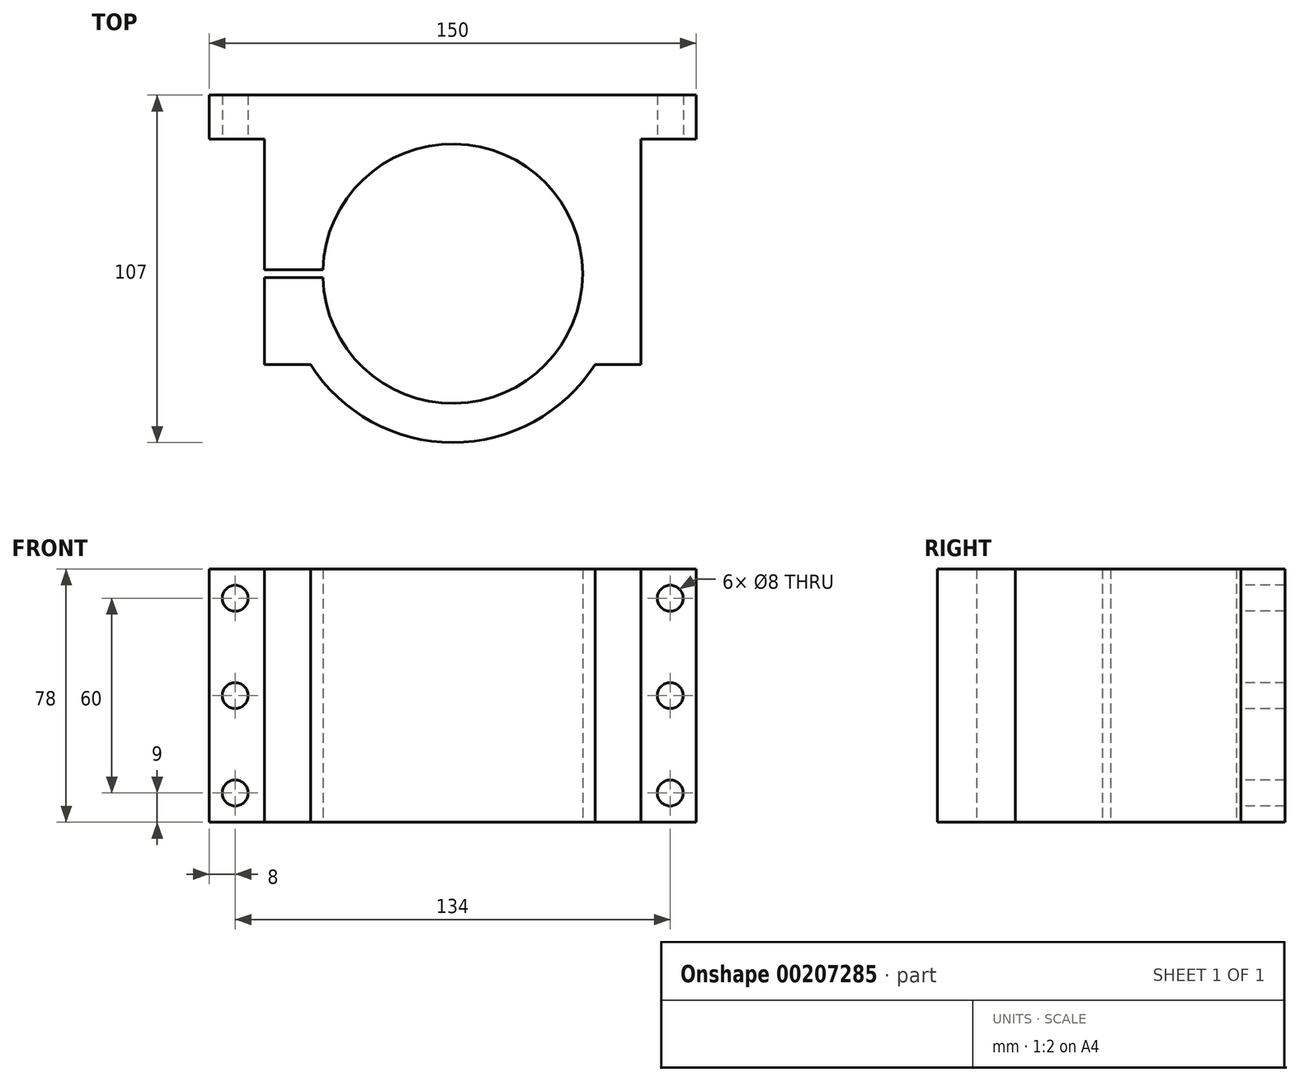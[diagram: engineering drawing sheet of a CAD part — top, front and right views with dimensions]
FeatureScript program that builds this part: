
annotation { "Feature Type Name" : "Feature", "Feature Type Description" : "" }
export const myFeature = defineFeature(function(context is Context, id is Id, definition is map)
    precondition{}
    {
        {
            var Q0;
            Q0=qCreatedBy(makeId("Top.planeOp"),FACE);
            var sketch = newSketch(context, id + "F0", { "sketchPlane" : qUnion([Q0])});
            skArc(sketch, "E0", {"start": v(-39.98, -1.25) * mm, "mid": v(40, 0) * mm, "end": v(-39.98, 1.25) * mm});
            skArc(sketch, "E1", {"start": v(-43.82, -28) * mm, "mid": v(0, -52) * mm, "end": v(43.82, -28) * mm});
            skLineSegment(sketch, "E2", {"start": v(-75, 55) * mm, "end": v(75, 55) * mm});
            skLineSegment(sketch, "E3", {"start": v(75, 55) * mm, "end": v(75, 41.5) * mm});
            skLineSegment(sketch, "E4", {"start": v(75, 41.5) * mm, "end": v(58, 41.5) * mm});
            skLineSegment(sketch, "E5", {"start": v(58, 41.5) * mm, "end": v(58, -28) * mm});
            skLineSegment(sketch, "E6", {"start": v(58, -28) * mm, "end": v(43.82, -28) * mm});
            skLineSegment(sketch, "E7", {"start": v(-58, -28) * mm, "end": v(-58, -1.25) * mm});
            skLineSegment(sketch, "E8", {"start": v(-58, 41.5) * mm, "end": v(-75, 41.5) * mm});
            skLineSegment(sketch, "E9", {"start": v(-75, 41.5) * mm, "end": v(-75, 55) * mm});
            skLineSegment(sketch, "E10", {"start": v(0, 0) * mm, "end": v(0, 55) * mm, "construction": true});
            skLineSegment(sketch, "E11.trimOffspring", {"start": v(-43.82, -28) * mm, "end": v(-58, -28) * mm});
            skLineSegment(sketch, "E12", {"start": v(-58, 1.25) * mm, "end": v(-39.98, 1.25) * mm});
            skLineSegment(sketch, "E13", {"start": v(-58, -1.25) * mm, "end": v(-39.98, -1.25) * mm});
            skLineSegment(sketch, "E14.trimOffspring", {"start": v(-58, 1.25) * mm, "end": v(-58, 41.5) * mm});
            skLineSegment(sketch, "E15", {"start": v(-58, 1.25) * mm, "end": v(-58, -1.25) * mm, "construction": true});
            skLineSegment(sketch, "E16", {"start": v(-58, 0) * mm, "end": v(0, 0) * mm, "construction": true});
            skSolve(sketch);
        }
        {
            var Q0;
            Q0 = qSketchRegion(id + "F0", true);
            extrude(context, id + "F1", {"entities" : qUnion([Q0]), "depth" : 78 * mm});
        }
        {
            var Q0;
            Q0=makeQuery(id+"F1.opExtrude","SWEPT_FACE",FACE,{"disambiguationData":[OSD([sQuery(id+"F0.wireOp",EDGE,"E4")])]});
            var sketch = newSketch(context, id + "F2", { "sketchPlane" : qUnion([Q0])});
            skLineSegment(sketch, "E17.bottom", {"start": v(-67, 69) * mm, "end": v(67, 69) * mm, "construction": true});
            skLineSegment(sketch, "E17.top", {"start": v(-67, 9) * mm, "end": v(67, 9) * mm, "construction": true});
            skLineSegment(sketch, "E17.left", {"start": v(-67, 69) * mm, "end": v(-67, 9) * mm, "construction": true});
            skLineSegment(sketch, "E17.right", {"start": v(67, 69) * mm, "end": v(67, 9) * mm, "construction": true});
            skLineSegment(sketch, "E18", {"start": v(0, 78) * mm, "end": v(0, 0) * mm, "construction": true});
            skLineSegment(sketch, "E19", {"start": v(-75, 39) * mm, "end": v(75, 39) * mm, "construction": true});
            skCircle(sketch, "E20", {"center": v(-67, 69) * mm, "radius": 4 * mm});
            skCircle(sketch, "E21", {"center": v(-67, 39) * mm, "radius": 4 * mm});
            skCircle(sketch, "E22", {"center": v(-67, 9) * mm, "radius": 4 * mm});
            skCircle(sketch, "E23", {"center": v(67, 9) * mm, "radius": 4 * mm});
            skCircle(sketch, "E24", {"center": v(67, 39) * mm, "radius": 4 * mm});
            skCircle(sketch, "E25", {"center": v(67, 69) * mm, "radius": 4 * mm});
            skSolve(sketch);
        }
        {
            var Q0;
            Q0 = qSketchRegion(id + "F2", true);
            extrude(context, id + "F3", {"entities" : qUnion([Q0]), "operationType" : NewBodyOperationType.REMOVE, "endBound" : BoundingType.THROUGH_ALL, "oppositeDirection" : true, "depth" : 25 * mm});
        }
    });
